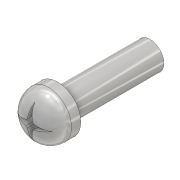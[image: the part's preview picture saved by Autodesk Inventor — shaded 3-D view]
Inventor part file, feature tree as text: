
AUTODESK INVENTOR PART (.ipt)
format: ipt  version: 2018 (Build 220112000, 112)  size: 151,552 bytes
history: native  units: mm
features: extrude x4, sketch x4, projected_geometry x2, fillet x1, mirror x1, pattern_circular x1
ambient origin geometry x8: Origin, YZ Plane, XZ Plane, XY Plane, X Axis, Y Axis, Z Axis, Center Point
bodies: Solid1 (feature_tree)
feature tree (13):
  extrude  "Extrusion1"  Depth=10.0mm TaperAngle=0.0deg
  extrude  "Extrusion2"  Depth=3.0mm TaperAngle=0.0deg
  fillet  "Fillet1"  Radius=2.0mm
  extrude  "Extrusion3"  TaperAngle=0.0deg  [1 undecoded]
  mirror  "Mirror1"
  pattern_circular  "Circular Pattern1"  Count=4 Angle=360.0deg
  extrude  "Extrusion4"  [1 undecoded]
  sketch  "Sketch1"  dims[d0=3.0mm d1=10.0mm d2=0.0mm]
  sketch  "Sketch2"  dims[d3=5.0mm d4=3.0mm d5=0.0mm d6=2.0mm]
  sketch  "Sketch3"  dims[d7=2.0mm d8=0.0mm d9=0.0mm d10=40.0mm d11=360.0deg]
  projected_geometry  "Projected Loop1"
  sketch  "Sketch4"  dims[d13=2.0mm d14=0.0mm]
  projected_geometry  "Projected Loop2"
note: 2 required parameter values undecoded (feature->parameter linkage not recoverable at this tier; creation-order binding heuristic only, values carry confidence <= 0.55)
